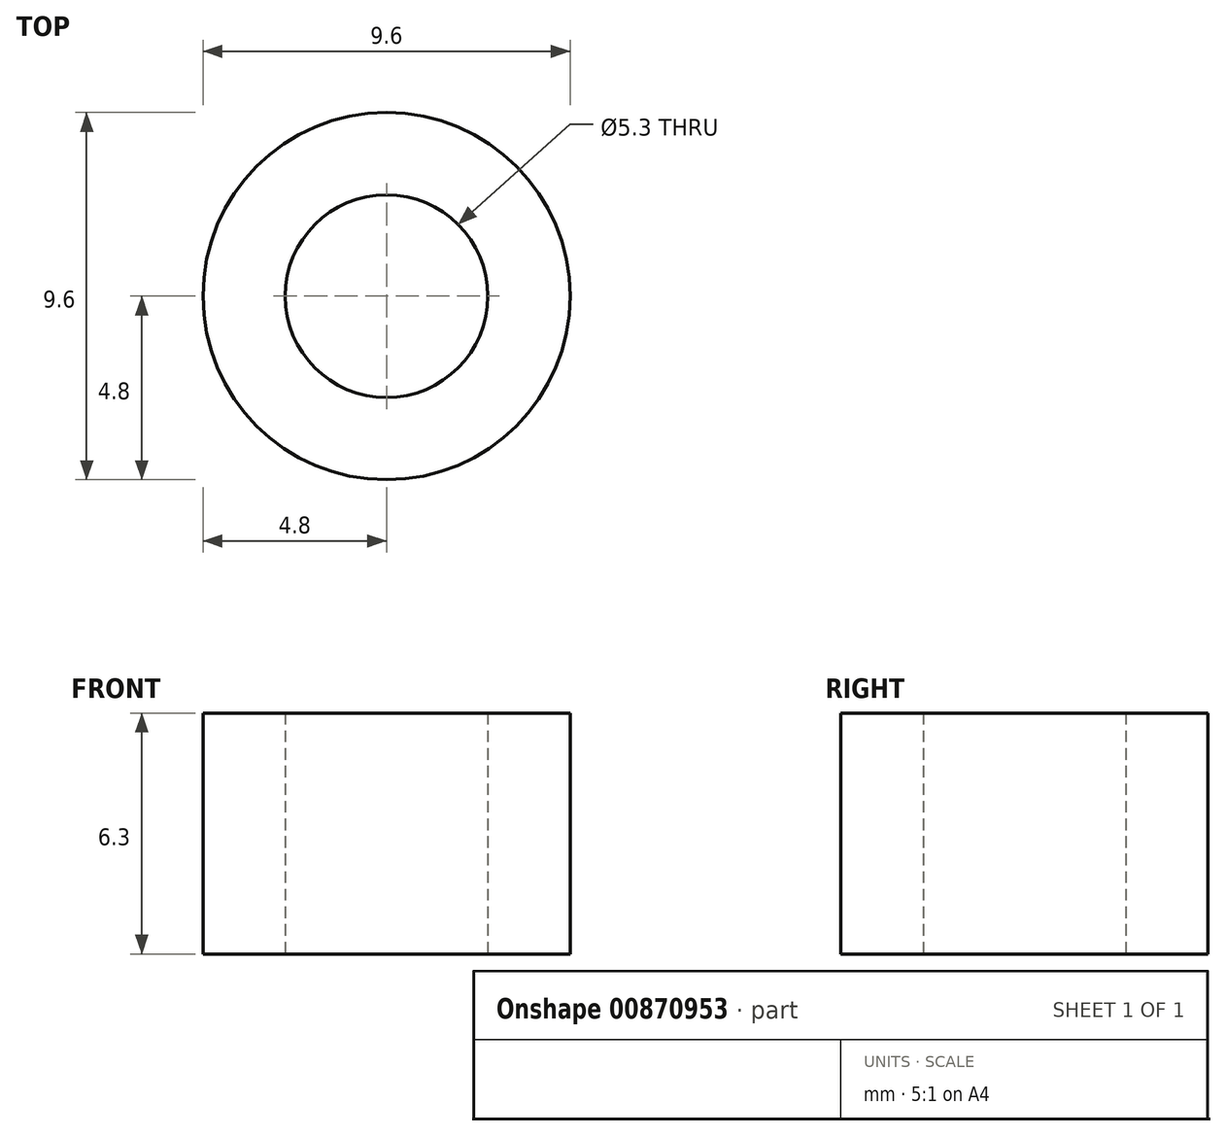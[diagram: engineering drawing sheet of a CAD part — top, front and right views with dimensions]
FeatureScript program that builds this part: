
annotation { "Feature Type Name" : "Feature", "Feature Type Description" : "" }
export const myFeature = defineFeature(function(context is Context, id is Id, definition is map)
    precondition{}
    {
        {
            var Q0;
            Q0=qCreatedBy(makeId("Top.planeOp"),FACE);
            var sketch = newSketch(context, id + "F0", { "sketchPlane" : qUnion([Q0])});
            skCircle(sketch, "E0", {"center": v(0, 0) * mm, "radius": 4.8 * mm});
            skCircle(sketch, "E1", {"center": v(0, 0) * mm, "radius": 2.65 * mm});
            skSolve(sketch);
        }
        {
            var Q0;
            Q0=makeQuery(id+"F0.imprint","IMPRINT",FACE,{"disambiguationData":[TD([[makeQuery(id+"F0.imprint","IMPRINT",EDGE,{"derivedFrom":sQuery(id+"F0.wireOp",EDGE,"E0")}),1.0]])]});
            extrude(context, id + "F1", {"entities" : qUnion([Q0]), "depth" : 6.3 * mm, "offsetDistance" : 25 * mm});
        }
    });
